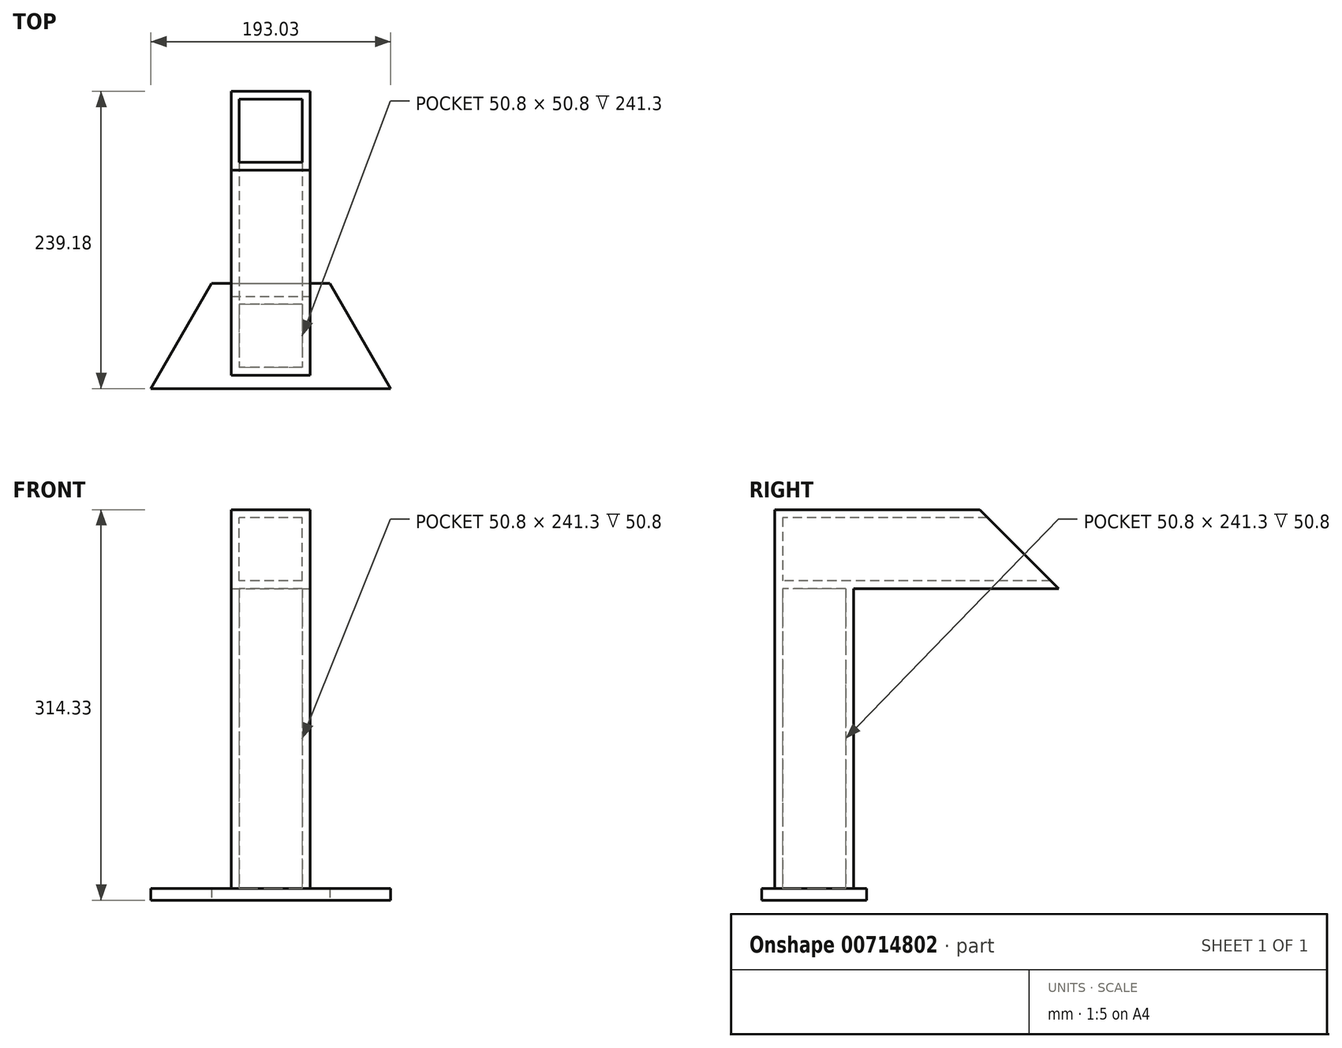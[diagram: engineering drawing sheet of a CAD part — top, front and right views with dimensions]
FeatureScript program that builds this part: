
annotation { "Feature Type Name" : "Feature", "Feature Type Description" : "" }
export const myFeature = defineFeature(function(context is Context, id is Id, definition is map)
    precondition{}
    {
        {
            var Q0;
            Q0=qCreatedBy(makeId("Top.planeOp"),FACE);
            var sketch = newSketch(context, id + "F0", { "sketchPlane" : qUnion([Q0])});
            skLineSegment(sketch, "E0", {"start": v(95.25, 0) * mm, "end": v(144.14, -84.67) * mm});
            skLineSegment(sketch, "E1", {"start": v(144.14, -84.67) * mm, "end": v(-48.89, -84.67) * mm});
            skLineSegment(sketch, "E2", {"start": v(0, 0) * mm, "end": v(-48.89, -84.67) * mm});
            skLineSegment(sketch, "E3", {"start": v(0, 0) * mm, "end": v(95.25, 0) * mm});
            skSolve(sketch);
        }
        {
            var Q0;
            Q0=makeQuery(id+"F0.imprint","IMPRINT",FACE,{"disambiguationData":[TD([[makeQuery(id+"F0.imprint","IMPRINT",EDGE,{"derivedFrom":sQuery(id+"F0.wireOp",EDGE,"E0")}),-1.0]])]});
            var sketch = newSketch(context, id + "F1", { "sketchPlane" : qUnion([Q0])});
            skSolve(sketch);
        }
        {
            var Q0;
            Q0=makeQuery(id+"F1.imprint","IMPRINT",FACE,{"disambiguationData":[TD([[makeQuery(id+"F1.imprint","IMPRINT",EDGE,{"derivedFrom":makeQuery(id+"F0.imprint","IMPRINT",EDGE,{"derivedFrom":sQuery(id+"F0.wireOp",EDGE,"E0")})}),-1.0]])]});
            extrude(context, id + "F2", {"entities" : qUnion([Q0]), "depth" : 9.52 * mm, "offsetDistance" : 25.4 * mm});
        }
        {
            var Q0;
            Q0=makeQuery(id+"F2.opExtrude","CAP_FACE",FACE,{"disambiguationData":[OSD([sQuery(id+"F0.wireOp",EDGE,"E0"),sQuery(id+"F0.wireOp",EDGE,"E1"),sQuery(id+"F0.wireOp",EDGE,"E2"),sQuery(id+"F0.wireOp",EDGE,"E3")])],"isStart":false});
            var sketch = newSketch(context, id + "F3", { "sketchPlane" : qUnion([Q0])});
            skLineSegment(sketch, "E4", {"start": v(95.25, 0) * mm, "end": v(47.62, 0) * mm});
            skLineSegment(sketch, "E5", {"start": v(47.62, 0) * mm, "end": v(47.63, -84.67) * mm});
            skLineSegment(sketch, "E6.bottom", {"start": v(15.88, -10.59) * mm, "end": v(79.38, -10.59) * mm});
            skLineSegment(sketch, "E6.top", {"start": v(15.87, -74.09) * mm, "end": v(79.38, -74.09) * mm});
            skLineSegment(sketch, "E6.left", {"start": v(15.88, -10.59) * mm, "end": v(15.87, -74.09) * mm});
            skLineSegment(sketch, "E6.right", {"start": v(79.38, -10.59) * mm, "end": v(79.38, -74.09) * mm});
            skPoint(sketch, "E6.middle", {"position": v(47.63, -42.34) * mm});
            skLineSegment(sketch, "E7.bottom", {"start": v(73.02, -16.94) * mm, "end": v(22.22, -16.94) * mm});
            skLineSegment(sketch, "E7.top", {"start": v(73.02, -67.74) * mm, "end": v(22.22, -67.74) * mm});
            skLineSegment(sketch, "E7.left", {"start": v(73.02, -16.94) * mm, "end": v(73.02, -67.74) * mm});
            skLineSegment(sketch, "E7.right", {"start": v(22.22, -16.94) * mm, "end": v(22.22, -67.74) * mm});
            skSolve(sketch);
        }
        {
            var Q0;
            Q0 = qSketchRegion(id + "F3", true);
            extrude(context, id + "F4", {"entities" : qUnion([Q0]), "operationType" : NewBodyOperationType.ADD, "depth" : 304.8 * mm, "offsetDistance" : 25.4 * mm});
        }
        {
            var Q0;
            Q0=makeQuery(id+"F4.opExtrude","SWEPT_FACE",FACE,{"disambiguationData":[OSD([sQuery(id+"F3.wireOp",EDGE,"E6.right")])]});
            var sketch = newSketch(context, id + "F5", { "sketchPlane" : qUnion([Q0])});
            skLineSegment(sketch, "E8", {"start": v(-74.09, 314.33) * mm, "end": v(-10.59, 250.82) * mm});
            skLineSegment(sketch, "E9", {"start": v(-10.59, 250.82) * mm, "end": v(-10.59, 314.33) * mm});
            skLineSegment(sketch, "E10", {"start": v(-10.59, 314.33) * mm, "end": v(-74.09, 314.33) * mm});
            skSolve(sketch);
        }
        {
            var Q0;
            Q0 = qSketchRegion(id + "F5", true);
            extrude(context, id + "F6", {"entities" : qUnion([Q0]), "operationType" : NewBodyOperationType.REMOVE, "oppositeDirection" : true, "depth" : 63.5 * mm, "offsetDistance" : 25.4 * mm});
        }
        {
            var Q0;
            Q0=makeQuery(id+"F6.boolean.opBoolean","COPY",FACE,{"derivedFrom":makeQuery(id+"F6.opExtrude","SWEPT_FACE",FACE,{"disambiguationData":[OSD([sQuery(id+"F5.wireOp",EDGE,"E8")])]})});
            var sketch = newSketch(context, id + "F7", { "sketchPlane" : qUnion([Q0])});
            skLineSegment(sketch, "E11.bottom", {"start": v(73.02, -265.67) * mm, "end": v(22.22, -265.67) * mm});
            skLineSegment(sketch, "E11.top", {"start": v(73.02, -193.83) * mm, "end": v(22.22, -193.83) * mm});
            skLineSegment(sketch, "E11.left", {"start": v(73.02, -265.67) * mm, "end": v(73.02, -193.83) * mm});
            skLineSegment(sketch, "E11.right", {"start": v(22.22, -265.67) * mm, "end": v(22.22, -193.83) * mm});
            skLineSegment(sketch, "E12.bottom", {"start": v(79.37, -274.65) * mm, "end": v(15.87, -274.65) * mm});
            skLineSegment(sketch, "E12.top", {"start": v(79.37, -184.85) * mm, "end": v(15.87, -184.85) * mm});
            skLineSegment(sketch, "E12.left", {"start": v(79.37, -274.65) * mm, "end": v(79.37, -184.85) * mm});
            skLineSegment(sketch, "E12.right", {"start": v(15.87, -274.65) * mm, "end": v(15.87, -184.85) * mm});
            skSolve(sketch);
        }
        {
            var Q0;
            Q0=makeQuery(id+"F4.opExtrude","SWEPT_FACE",FACE,{"disambiguationData":[OSD([sQuery(id+"F3.wireOp",EDGE,"E6.top")])]});
            var sketch = newSketch(context, id + "F8", { "sketchPlane" : qUnion([Q0])});
            skLineSegment(sketch, "E13.0", {"start": v(22.22, 307.98) * mm, "end": v(22.22, 257.18) * mm});
            skLineSegment(sketch, "E14.0", {"start": v(73.02, 307.98) * mm, "end": v(22.22, 307.98) * mm});
            skLineSegment(sketch, "E15.0", {"start": v(73.02, 307.98) * mm, "end": v(73.02, 257.18) * mm});
            skLineSegment(sketch, "E16.0", {"start": v(73.02, 257.18) * mm, "end": v(22.22, 257.18) * mm});
            skLineSegment(sketch, "E17.0", {"start": v(79.38, 314.33) * mm, "end": v(15.88, 314.33) * mm});
            skLineSegment(sketch, "E18.0", {"start": v(79.38, 250.82) * mm, "end": v(15.88, 250.82) * mm});
            skLineSegment(sketch, "E19.bottom", {"start": v(15.88, 314.33) * mm, "end": v(79.38, 314.33) * mm});
            skLineSegment(sketch, "E19.top", {"start": v(15.88, 250.82) * mm, "end": v(79.38, 250.82) * mm});
            skLineSegment(sketch, "E19.left", {"start": v(15.88, 314.33) * mm, "end": v(15.88, 250.82) * mm});
            skLineSegment(sketch, "E19.right", {"start": v(79.38, 314.33) * mm, "end": v(79.38, 250.82) * mm});
            skSolve(sketch);
        }
        {
            var Q0;
            Q0=makeQuery(id+"F8.imprint","IMPRINT",FACE,{"disambiguationData":[TD([[makeQuery(id+"F8.imprint","IMPRINT",EDGE,{"derivedFrom":sQuery(id+"F8.wireOp",EDGE,"E13.0")}),-1.0]])]});
            extrude(context, id + "F9", {"entities" : qUnion([Q0]), "operationType" : NewBodyOperationType.ADD, "oppositeDirection" : true, "depth" : 228.6 * mm, "offsetDistance" : 25.4 * mm});
        }
        {
            var Q0;
            Q0=makeQuery(id+"F9.boolean.opBoolean","MERGE",FACE,{"derivedFrom":[makeQuery(id+"F4.opExtrude","SWEPT_FACE",FACE,{"disambiguationData":[OSD([sQuery(id+"F3.wireOp",EDGE,"E6.right")])]}),makeQuery(id+"F9.opExtrude","SWEPT_FACE",FACE,{"disambiguationData":[OSD([sQuery(id+"F8.wireOp",EDGE,"E19.right")])]})]});
            var sketch = newSketch(context, id + "F10", { "sketchPlane" : qUnion([Q0])});
            skLineSegment(sketch, "E20", {"start": v(154.51, 250.82) * mm, "end": v(91.01, 314.33) * mm});
            skLineSegment(sketch, "E21", {"start": v(91.01, 314.33) * mm, "end": v(154.51, 314.33) * mm});
            skLineSegment(sketch, "E22", {"start": v(154.51, 314.33) * mm, "end": v(154.51, 250.82) * mm});
            skSolve(sketch);
        }
        {
            var Q0;
            Q0 = qSketchRegion(id + "F10", true);
            extrude(context, id + "F11", {"entities" : qUnion([Q0]), "operationType" : NewBodyOperationType.REMOVE, "endBound" : BoundingType.THROUGH_ALL, "oppositeDirection" : true, "depth" : 25.4 * mm, "offsetDistance" : 25.4 * mm});
        }
    });
